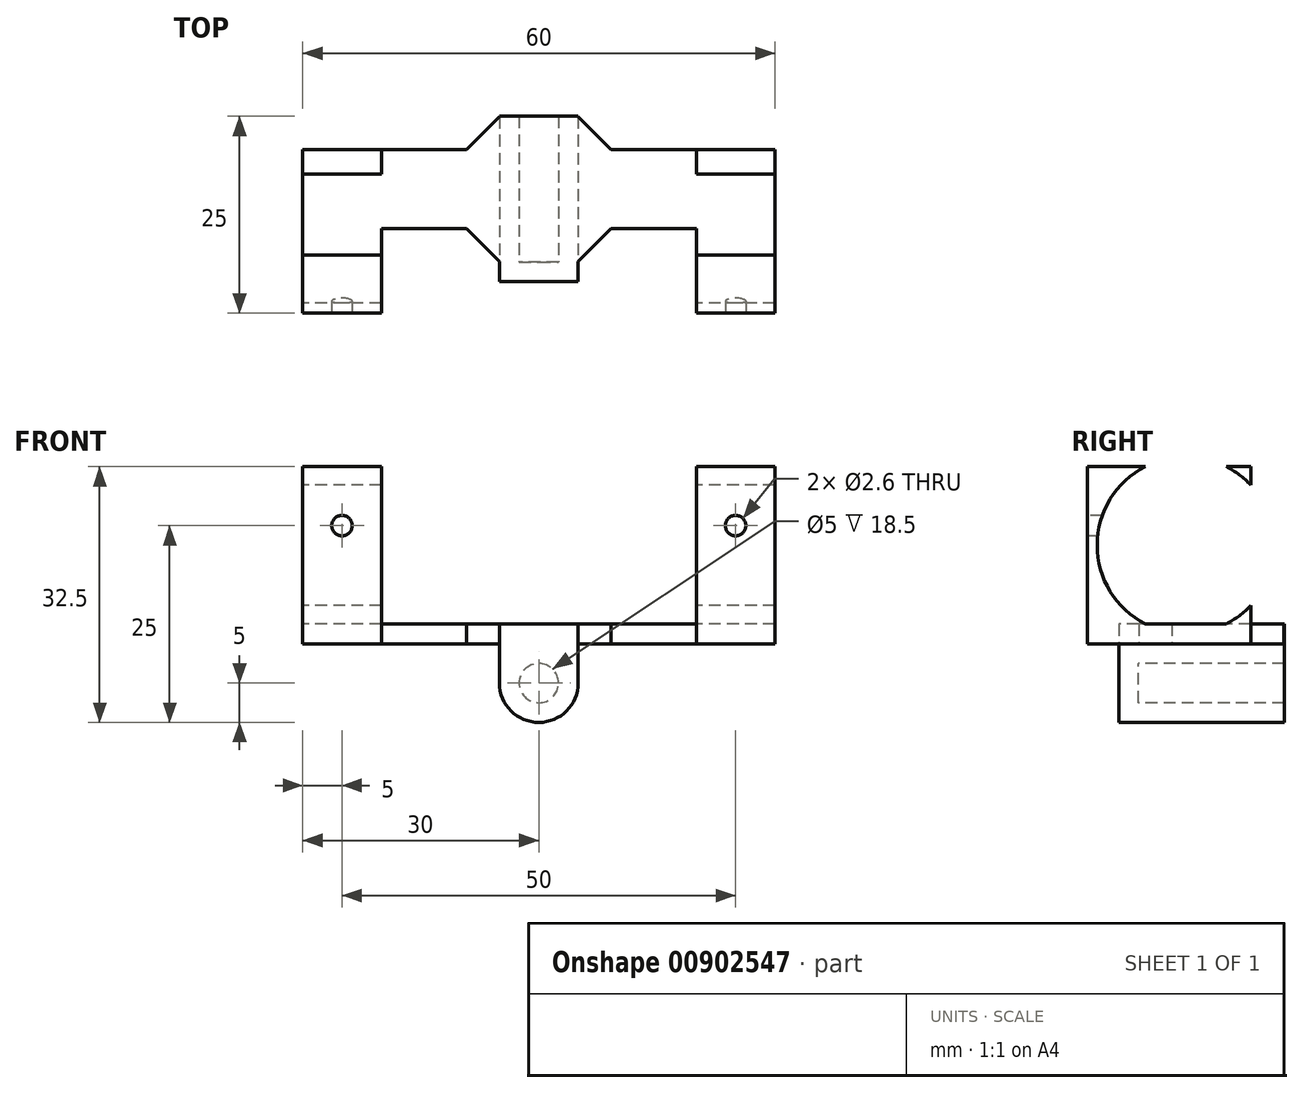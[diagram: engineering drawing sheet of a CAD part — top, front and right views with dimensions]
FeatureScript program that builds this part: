
annotation { "Feature Type Name" : "Feature", "Feature Type Description" : "" }
export const myFeature = defineFeature(function(context is Context, id is Id, definition is map)
    precondition{}
    {
        {
            var Q0;
            Q0=qCreatedBy(makeId("Top.planeOp"),FACE);
            var sketch = newSketch(context, id + "F0", { "sketchPlane" : qUnion([Q0])});
            skLineSegment(sketch, "E0.bottom", {"start": v(5, 9.25) * mm, "end": v(-5, 9.25) * mm});
            skLineSegment(sketch, "E0.top", {"start": v(5, -9.25) * mm, "end": v(-5, -9.25) * mm});
            skLineSegment(sketch, "E0.left", {"start": v(5, 9.25) * mm, "end": v(5, -9.25) * mm});
            skLineSegment(sketch, "E0.right", {"start": v(-5, 9.25) * mm, "end": v(-5, -9.25) * mm});
            skPoint(sketch, "E0.middle", {"position": v(0, 0) * mm});
            skLineSegment(sketch, "E1.bottom", {"start": v(30, 5) * mm, "end": v(-30, 5) * mm});
            skLineSegment(sketch, "E1.top", {"start": v(30, -5) * mm, "end": v(-30, -5) * mm});
            skLineSegment(sketch, "E1.left", {"start": v(30, 5) * mm, "end": v(30, -5) * mm});
            skLineSegment(sketch, "E1.right", {"start": v(-30, 5) * mm, "end": v(-30, -5) * mm});
            skSolve(sketch);
        }
        {
            var Q0;
            {var subQ5=sQuery(id+"F0.wireOp",EDGE,"E1.right");Q0=makeQuery(id+"F0.imprint","IMPRINT",FACE,{"disambiguationData":[TD([[makeQuery(id+"F0.imprint","IMPRINT",EDGE,{"derivedFrom":subQ5}),1.0]])]});}
            var Q1;
            {var subQ0=sQuery(id+"F0.wireOp",EDGE,"E0.bottom");Q1=makeQuery(id+"F0.imprint","IMPRINT",FACE,{"disambiguationData":[TD([[makeQuery(id+"F0.imprint","IMPRINT",EDGE,{"derivedFrom":subQ0}),1.0]])]});}
            var Q2;
            {var subQ0=sQuery(id+"F0.wireOp",EDGE,"E1.bottom");var subQ1=sQuery(id+"F0.wireOp",EDGE,"E0.left");var subQ2=makeQuery(id+"F0.imprint","INTERSECT",VERTEX,{"derivedFrom":[subQ1,subQ0]});Q2=makeQuery(id+"F0.imprint","IMPRINT",FACE,{"disambiguationData":[TD([[makeQuery(id+"F0.imprint","IMPRINT",EDGE,{"disambiguationData":[TD([[subQ2,-1.0]])],"derivedFrom":subQ1}),-1.0]])]});}
            var Q3;
            {var subQ0=sQuery(id+"F0.wireOp",EDGE,"E0.top");Q3=makeQuery(id+"F0.imprint","IMPRINT",FACE,{"disambiguationData":[TD([[makeQuery(id+"F0.imprint","IMPRINT",EDGE,{"derivedFrom":subQ0}),-1.0]])]});}
            var Q4;
            {var subQ5=sQuery(id+"F0.wireOp",EDGE,"E1.left");Q4=makeQuery(id+"F0.imprint","IMPRINT",FACE,{"disambiguationData":[TD([[makeQuery(id+"F0.imprint","IMPRINT",EDGE,{"derivedFrom":subQ5}),-1.0]])]});}
            extrude(context, id + "F1", {"entities" : qUnion([Q0, Q1, Q2, Q3, Q4]), "depth" : 2.5 * mm, "offsetDistance" : 25 * mm});
        }
        {
            var Q0;
            Q0=makeQuery(id+"F1.opExtrude","SWEPT_FACE",FACE,{"disambiguationData":[OSD([sQuery(id+"F0.wireOp",EDGE,"E0.top")])]});
            var sketch = newSketch(context, id + "F2", { "sketchPlane" : qUnion([Q0])});
            skLineSegment(sketch, "E2.bottom", {"start": v(-5, 0) * mm, "end": v(5, 0) * mm});
            skLineSegment(sketch, "E2.top", {"start": v(-5, -5) * mm, "end": v(5, -5) * mm});
            skLineSegment(sketch, "E2.left", {"start": v(-5, 0) * mm, "end": v(-5, -5) * mm});
            skLineSegment(sketch, "E2.right", {"start": v(5, 0) * mm, "end": v(5, -5) * mm});
            skCircle(sketch, "E3", {"center": v(0, -5) * mm, "radius": 5 * mm});
            skCircle(sketch, "E4", {"center": v(0, -5) * mm, "radius": 2.5 * mm});
            skSolve(sketch);
        }
        {
            var Q0;
            Q0=makeQuery(id+"F2.imprint","IMPRINT",FACE,{"disambiguationData":[TD([[makeQuery(id+"F2.imprint","IMPRINT",EDGE,{"derivedFrom":sQuery(id+"F2.wireOp",EDGE,"E2.bottom")}),1.0]])]});
            var Q1;
            {var subQ1=sQuery(id+"F2.wireOp",EDGE,"E2.top");var subQ3=sQuery(id+"F2.wireOp",EDGE,"E4");var subQ4=makeQuery(id+"F2.imprint","INTERSECT",VERTEX,{"disambiguationData":[OD(0.0)],"derivedFrom":[subQ1,subQ3]});Q1=makeQuery(id+"F2.imprint","IMPRINT",FACE,{"disambiguationData":[TD([[makeQuery(id+"F2.imprint","IMPRINT",EDGE,{"disambiguationData":[TD([[subQ4,1.0]])],"derivedFrom":subQ3}),-1.0]])]});}
            var Q2;
            {var subQ1=sQuery(id+"F2.wireOp",EDGE,"E2.top");var subQ3=sQuery(id+"F2.wireOp",EDGE,"E4");var subQ4=makeQuery(id+"F2.imprint","INTERSECT",VERTEX,{"disambiguationData":[OD(0.0)],"derivedFrom":[subQ1,subQ3]});Q2=makeQuery(id+"F2.imprint","IMPRINT",FACE,{"disambiguationData":[TD([[makeQuery(id+"F2.imprint","IMPRINT",EDGE,{"disambiguationData":[TD([[subQ4,-1.0]])],"derivedFrom":subQ3}),-1.0]])]});}
            var Q3;
            {var subQ0=sQuery(id+"F2.wireOp",EDGE,"E4");var subQ1=sQuery(id+"F2.wireOp",EDGE,"E2.top");var subQ2=makeQuery(id+"F2.imprint","INTERSECT",VERTEX,{"disambiguationData":[OD(0.0)],"derivedFrom":[subQ1,subQ0]});Q3=makeQuery(id+"F2.imprint","IMPRINT",FACE,{"disambiguationData":[TD([[makeQuery(id+"F2.imprint","IMPRINT",EDGE,{"disambiguationData":[TD([[subQ2,-1.0]])],"derivedFrom":subQ1}),-1.0]])]});}
            var Q4;
            {var subQ0=sQuery(id+"F2.wireOp",EDGE,"E4");var subQ1=sQuery(id+"F2.wireOp",EDGE,"E2.top");var subQ2=makeQuery(id+"F2.imprint","INTERSECT",VERTEX,{"disambiguationData":[OD(0.0)],"derivedFrom":[subQ1,subQ0]});Q4=makeQuery(id+"F2.imprint","IMPRINT",FACE,{"disambiguationData":[TD([[makeQuery(id+"F2.imprint","IMPRINT",EDGE,{"disambiguationData":[TD([[subQ2,-1.0]])],"derivedFrom":subQ1}),1.0]])]});}
            var Q5;
            Q5=makeQuery(id+"F2.imprint","IMPRINT",FACE,{"disambiguationData":[TD([[makeQuery(id+"F2.imprint","IMPRINT",EDGE,{"derivedFrom":sQuery(id+"F2.wireOp",EDGE,"E2.bottom")}),-1.0]])]});
            extrude(context, id + "F3", {"entities" : qUnion([Q0, Q1, Q2, Q3, Q4, Q5]), "operationType" : NewBodyOperationType.ADD, "depth" : 2.5 * mm, "offsetDistance" : 25 * mm});
        }
        {
            var Q0;
            {var subQ1=sQuery(id+"F2.wireOp",EDGE,"E2.top");var subQ3=sQuery(id+"F2.wireOp",EDGE,"E4");var subQ4=makeQuery(id+"F2.imprint","INTERSECT",VERTEX,{"disambiguationData":[OD(0.0)],"derivedFrom":[subQ1,subQ3]});Q0=makeQuery(id+"F2.imprint","IMPRINT",FACE,{"disambiguationData":[TD([[makeQuery(id+"F2.imprint","IMPRINT",EDGE,{"disambiguationData":[TD([[subQ4,1.0]])],"derivedFrom":subQ3}),-1.0]])]});}
            var Q1;
            {var subQ1=sQuery(id+"F2.wireOp",EDGE,"E2.top");var subQ3=sQuery(id+"F2.wireOp",EDGE,"E4");var subQ4=makeQuery(id+"F2.imprint","INTERSECT",VERTEX,{"disambiguationData":[OD(0.0)],"derivedFrom":[subQ1,subQ3]});Q1=makeQuery(id+"F2.imprint","IMPRINT",FACE,{"disambiguationData":[TD([[makeQuery(id+"F2.imprint","IMPRINT",EDGE,{"disambiguationData":[TD([[subQ4,-1.0]])],"derivedFrom":subQ3}),-1.0]])]});}
            var Q2;
            Q2=makeQuery(id+"F2.imprint","IMPRINT",FACE,{"disambiguationData":[TD([[makeQuery(id+"F2.imprint","IMPRINT",EDGE,{"derivedFrom":sQuery(id+"F2.wireOp",EDGE,"E2.bottom")}),1.0]])]});
            extrude(context, id + "F4", {"entities" : qUnion([Q0, Q1, Q2]), "operationType" : NewBodyOperationType.ADD, "oppositeDirection" : true, "depth" : 18.5 * mm, "offsetDistance" : 25 * mm});
        }
        {
            var Q0;
            Q0=makeQuery(id+"F1.opExtrude","SWEPT_EDGE",EDGE,{"disambiguationData":[OSD([sQuery(id+"F0.wireOp",EDGE,"E0.right"),sQuery(id+"F0.wireOp",EDGE,"E1.bottom")])]});
            var Q1;
            Q1=makeQuery(id+"F1.opExtrude","SWEPT_EDGE",EDGE,{"disambiguationData":[OSD([sQuery(id+"F0.wireOp",EDGE,"E0.right"),sQuery(id+"F0.wireOp",EDGE,"E1.top")])]});
            var Q2;
            Q2=makeQuery(id+"F1.opExtrude","SWEPT_EDGE",EDGE,{"disambiguationData":[OSD([sQuery(id+"F0.wireOp",EDGE,"E0.left"),sQuery(id+"F0.wireOp",EDGE,"E1.bottom")])]});
            var Q3;
            Q3=makeQuery(id+"F1.opExtrude","SWEPT_EDGE",EDGE,{"disambiguationData":[OSD([sQuery(id+"F0.wireOp",EDGE,"E0.left"),sQuery(id+"F0.wireOp",EDGE,"E1.top")])]});
            chamfer(context, id + "F5", {"entities" : qUnion([Q0, Q1, Q2, Q3]), "width" : 4.2 * mm, "tangentPropagation" : true});
        }
        {
            var Q0;
            {var subQ0=sQuery(id+"F0.wireOp",EDGE,"E0.top");Q0=makeQuery(id+"F3.boolean.opBoolean","MERGE",FACE,{"derivedFrom":[makeQuery(id+"F1.opExtrude","CAP_FACE",FACE,{"disambiguationData":[OSD([sQuery(id+"F0.wireOp",EDGE,"E0.bottom"),subQ0,sQuery(id+"F0.wireOp",EDGE,"E0.left"),sQuery(id+"F0.wireOp",EDGE,"E0.right"),sQuery(id+"F0.wireOp",EDGE,"E1.bottom"),sQuery(id+"F0.wireOp",EDGE,"E1.top"),sQuery(id+"F0.wireOp",EDGE,"E1.left"),sQuery(id+"F0.wireOp",EDGE,"E1.right")])],"isStart":false}),makeQuery(id+"F3.opExtrude","SWEPT_FACE",FACE,{"disambiguationData":[OSD([subQ0])]})]});}
            var sketch = newSketch(context, id + "F6", { "sketchPlane" : qUnion([Q0])});
            skLineSegment(sketch, "E5", {"start": v(0, 9.25) * mm, "end": v(-30, 9.25) * mm});
            skLineSegment(sketch, "E6.bottom", {"start": v(-30, 9.25) * mm, "end": v(-20, 9.25) * mm});
            skLineSegment(sketch, "E6.top", {"start": v(-30, -15.75) * mm, "end": v(-20, -15.75) * mm});
            skLineSegment(sketch, "E6.left", {"start": v(-30, 9.25) * mm, "end": v(-30, -15.75) * mm});
            skLineSegment(sketch, "E6.right", {"start": v(-20, 9.25) * mm, "end": v(-20, -15.75) * mm});
            skLineSegment(sketch, "E7", {"start": v(0, 9.25) * mm, "end": v(30, 9.25) * mm});
            skLineSegment(sketch, "E8.bottom", {"start": v(30, 9.25) * mm, "end": v(20, 9.25) * mm});
            skLineSegment(sketch, "E8.top", {"start": v(30, -15.75) * mm, "end": v(20, -15.75) * mm});
            skLineSegment(sketch, "E8.left", {"start": v(30, 9.25) * mm, "end": v(30, -15.75) * mm});
            skLineSegment(sketch, "E8.right", {"start": v(20, 9.25) * mm, "end": v(20, -15.75) * mm});
            skSolve(sketch);
        }
        {
            var Q0;
            {var subQ0=sQuery(id+"F6.wireOp",EDGE,"E6.bottom");Q0=makeQuery(id+"F6.imprint","IMPRINT",FACE,{"disambiguationData":[TD([[makeQuery(id+"F6.imprint","IMPRINT",EDGE,{"derivedFrom":subQ0}),-1.0]])]});}
            var Q1;
            {var subQ0=sQuery(id+"F6.wireOp",EDGE,"E6.left");var subQ1=sQuery(id+"F0.wireOp",EDGE,"E1.right");var subQ2=sQuery(id+"F0.wireOp",EDGE,"E1.bottom");var subQ4=makeQuery(id+"F1.opExtrude","CAP_EDGE",EDGE,{"disambiguationData":[OSD([subQ2]),TDD([makeQuery(id+"F0.imprint","IMPRINT",EDGE,{"disambiguationData":[TD([[makeQuery(id+"F0.imprint","INTERSECT",VERTEX,{"derivedFrom":[subQ2,subQ1]}),1.0]])],"derivedFrom":subQ2})])],"isStart":false});var subQ5=makeQuery(id+"F6.imprint","INTERSECT",VERTEX,{"derivedFrom":[subQ4,subQ0]});Q1=makeQuery(id+"F6.imprint","IMPRINT",FACE,{"disambiguationData":[TD([[makeQuery(id+"F6.imprint","IMPRINT",EDGE,{"disambiguationData":[TD([[subQ5,-1.0]])],"derivedFrom":subQ0}),1.0]])]});}
            var Q2;
            {var subQ0=sQuery(id+"F6.wireOp",EDGE,"E6.top");Q2=makeQuery(id+"F6.imprint","IMPRINT",FACE,{"disambiguationData":[TD([[makeQuery(id+"F6.imprint","IMPRINT",EDGE,{"derivedFrom":subQ0}),1.0]])]});}
            var Q3;
            {var subQ0=sQuery(id+"F6.wireOp",EDGE,"E8.bottom");Q3=makeQuery(id+"F6.imprint","IMPRINT",FACE,{"disambiguationData":[TD([[makeQuery(id+"F6.imprint","IMPRINT",EDGE,{"derivedFrom":subQ0}),1.0]])]});}
            var Q4;
            {var subQ0=sQuery(id+"F6.wireOp",EDGE,"E8.left");var subQ1=sQuery(id+"F0.wireOp",EDGE,"E1.left");var subQ2=sQuery(id+"F0.wireOp",EDGE,"E1.bottom");var subQ4=makeQuery(id+"F1.opExtrude","CAP_EDGE",EDGE,{"disambiguationData":[OSD([subQ2]),TDD([makeQuery(id+"F0.imprint","IMPRINT",EDGE,{"disambiguationData":[TD([[makeQuery(id+"F0.imprint","INTERSECT",VERTEX,{"derivedFrom":[subQ2,subQ1]}),-1.0]])],"derivedFrom":subQ2})])],"isStart":false});var subQ5=makeQuery(id+"F6.imprint","INTERSECT",VERTEX,{"derivedFrom":[subQ4,subQ0]});Q4=makeQuery(id+"F6.imprint","IMPRINT",FACE,{"disambiguationData":[TD([[makeQuery(id+"F6.imprint","IMPRINT",EDGE,{"disambiguationData":[TD([[subQ5,-1.0]])],"derivedFrom":subQ0}),-1.0]])]});}
            var Q5;
            {var subQ0=sQuery(id+"F6.wireOp",EDGE,"E8.top");Q5=makeQuery(id+"F6.imprint","IMPRINT",FACE,{"disambiguationData":[TD([[makeQuery(id+"F6.imprint","IMPRINT",EDGE,{"derivedFrom":subQ0}),-1.0]])]});}
            extrude(context, id + "F7", {"entities" : qUnion([Q0, Q1, Q2, Q3, Q4, Q5]), "operationType" : NewBodyOperationType.ADD, "oppositeDirection" : true, "depth" : 2.5 * mm, "offsetDistance" : 25 * mm});
        }
        {
            var Q0;
            {var subQ0=sQuery(id+"F6.wireOp",EDGE,"E6.bottom");Q0=makeQuery(id+"F6.imprint","IMPRINT",FACE,{"disambiguationData":[TD([[makeQuery(id+"F6.imprint","IMPRINT",EDGE,{"derivedFrom":subQ0}),-1.0]])]});}
            var Q1;
            {var subQ0=sQuery(id+"F6.wireOp",EDGE,"E6.left");var subQ1=sQuery(id+"F0.wireOp",EDGE,"E1.right");var subQ2=sQuery(id+"F0.wireOp",EDGE,"E1.bottom");var subQ4=makeQuery(id+"F1.opExtrude","CAP_EDGE",EDGE,{"disambiguationData":[OSD([subQ2]),TDD([makeQuery(id+"F0.imprint","IMPRINT",EDGE,{"disambiguationData":[TD([[makeQuery(id+"F0.imprint","INTERSECT",VERTEX,{"derivedFrom":[subQ2,subQ1]}),1.0]])],"derivedFrom":subQ2})])],"isStart":false});var subQ5=makeQuery(id+"F6.imprint","INTERSECT",VERTEX,{"derivedFrom":[subQ4,subQ0]});Q1=makeQuery(id+"F6.imprint","IMPRINT",FACE,{"disambiguationData":[TD([[makeQuery(id+"F6.imprint","IMPRINT",EDGE,{"disambiguationData":[TD([[subQ5,-1.0]])],"derivedFrom":subQ0}),1.0]])]});}
            var Q2;
            {var subQ0=sQuery(id+"F6.wireOp",EDGE,"E6.top");Q2=makeQuery(id+"F6.imprint","IMPRINT",FACE,{"disambiguationData":[TD([[makeQuery(id+"F6.imprint","IMPRINT",EDGE,{"derivedFrom":subQ0}),1.0]])]});}
            var Q3;
            {var subQ0=sQuery(id+"F6.wireOp",EDGE,"E8.top");Q3=makeQuery(id+"F6.imprint","IMPRINT",FACE,{"disambiguationData":[TD([[makeQuery(id+"F6.imprint","IMPRINT",EDGE,{"derivedFrom":subQ0}),-1.0]])]});}
            var Q4;
            {var subQ0=sQuery(id+"F6.wireOp",EDGE,"E8.left");var subQ1=sQuery(id+"F0.wireOp",EDGE,"E1.left");var subQ2=sQuery(id+"F0.wireOp",EDGE,"E1.bottom");var subQ4=makeQuery(id+"F1.opExtrude","CAP_EDGE",EDGE,{"disambiguationData":[OSD([subQ2]),TDD([makeQuery(id+"F0.imprint","IMPRINT",EDGE,{"disambiguationData":[TD([[makeQuery(id+"F0.imprint","INTERSECT",VERTEX,{"derivedFrom":[subQ2,subQ1]}),-1.0]])],"derivedFrom":subQ2})])],"isStart":false});var subQ5=makeQuery(id+"F6.imprint","INTERSECT",VERTEX,{"derivedFrom":[subQ4,subQ0]});Q4=makeQuery(id+"F6.imprint","IMPRINT",FACE,{"disambiguationData":[TD([[makeQuery(id+"F6.imprint","IMPRINT",EDGE,{"disambiguationData":[TD([[subQ5,-1.0]])],"derivedFrom":subQ0}),-1.0]])]});}
            var Q5;
            {var subQ0=sQuery(id+"F6.wireOp",EDGE,"E8.bottom");Q5=makeQuery(id+"F6.imprint","IMPRINT",FACE,{"disambiguationData":[TD([[makeQuery(id+"F6.imprint","IMPRINT",EDGE,{"derivedFrom":subQ0}),1.0]])]});}
            extrude(context, id + "F8", {"entities" : qUnion([Q0, Q1, Q2, Q3, Q4, Q5]), "operationType" : NewBodyOperationType.ADD, "depth" : 20 * mm, "offsetDistance" : 25 * mm});
        }
        {
            var Q0;
            {var subQ0=sQuery(id+"F6.wireOp",EDGE,"E6.left");Q0=makeQuery(id+"F8.boolean.opBoolean","MERGE",FACE,{"derivedFrom":[makeQuery(id+"F7.boolean.opBoolean","MERGE",FACE,{"derivedFrom":[makeQuery(id+"F1.opExtrude","SWEPT_FACE",FACE,{"disambiguationData":[OSD([sQuery(id+"F0.wireOp",EDGE,"E1.right")])]}),makeQuery(id+"F7.opExtrude","SWEPT_FACE",FACE,{"disambiguationData":[OSD([subQ0])]})]}),makeQuery(id+"F8.opExtrude","SWEPT_FACE",FACE,{"disambiguationData":[OSD([subQ0])]})]});}
            var sketch = newSketch(context, id + "F9", { "sketchPlane" : qUnion([Q0])});
            skLineSegment(sketch, "E9", {"start": v(3.25, 22.5) * mm, "end": v(3.25, 12.5) * mm});
            skCircle(sketch, "E10", {"center": v(3.25, 12.5) * mm, "radius": 11.25 * mm});
            skLineSegment(sketch, "E11.bottom", {"start": v(14.5, 22.5) * mm, "end": v(-8, 22.5) * mm});
            skLineSegment(sketch, "E11.top", {"start": v(14.5, 2.5) * mm, "end": v(-8, 2.5) * mm});
            skLineSegment(sketch, "E11.left", {"start": v(14.5, 22.5) * mm, "end": v(14.5, 2.5) * mm});
            skLineSegment(sketch, "E11.right", {"start": v(-8, 22.5) * mm, "end": v(-8, 2.5) * mm});
            skSolve(sketch);
        }
        {
            var Q0;
            {var subQ4=sQuery(id+"F9.wireOp",EDGE,"E11.bottom");var subQ9=makeQuery(id+"F9.imprint","IMPRINT",VERTEX,{"derivedFrom":subQ4});Q0=makeQuery(id+"F9.imprint","IMPRINT",FACE,{"disambiguationData":[TD([[makeQuery(id+"F9.imprint","IMPRINT",EDGE,{"disambiguationData":[TD([[subQ9,1.0]])],"derivedFrom":subQ4}),-1.0]])]});}
            var Q1;
            {var subQ0=sQuery(id+"F9.wireOp",EDGE,"E11.bottom");var subQ1=sQuery(id+"F9.wireOp",EDGE,"E10");var subQ2=makeQuery(id+"F9.imprint","INTERSECT",VERTEX,{"disambiguationData":[OD(1.0)],"derivedFrom":[subQ1,subQ0]});Q1=makeQuery(id+"F9.imprint","IMPRINT",FACE,{"disambiguationData":[TD([[makeQuery(id+"F9.imprint","IMPRINT",EDGE,{"disambiguationData":[TD([[subQ2,-1.0]])],"derivedFrom":subQ1}),-1.0]])]});}
            var Q2;
            {var subQ0=sQuery(id+"F9.wireOp",EDGE,"E11.bottom");var subQ1=sQuery(id+"F9.wireOp",EDGE,"E10");var subQ2=makeQuery(id+"F9.imprint","INTERSECT",VERTEX,{"disambiguationData":[OD(0.0)],"derivedFrom":[subQ1,subQ0]});Q2=makeQuery(id+"F9.imprint","IMPRINT",FACE,{"disambiguationData":[TD([[makeQuery(id+"F9.imprint","IMPRINT",EDGE,{"disambiguationData":[TD([[subQ2,1.0]])],"derivedFrom":subQ1}),-1.0]])]});}
            extrude(context, id + "F10", {"entities" : qUnion([Q0, Q1, Q2]), "operationType" : NewBodyOperationType.REMOVE, "oppositeDirection" : true, "depth" : 60 * mm, "offsetDistance" : 25 * mm});
        }
        {
            var Q0;
            {var subQ0=sQuery(id+"F6.wireOp",EDGE,"E6.top");Q0=makeQuery(id+"F8.boolean.opBoolean","MERGE",FACE,{"derivedFrom":[makeQuery(id+"F7.opExtrude","SWEPT_FACE",FACE,{"disambiguationData":[OSD([subQ0])]}),makeQuery(id+"F8.opExtrude","SWEPT_FACE",FACE,{"disambiguationData":[OSD([subQ0])]})]});}
            var sketch = newSketch(context, id + "F11", { "sketchPlane" : qUnion([Q0])});
            skLineSegment(sketch, "E12", {"start": v(-25, 22.5) * mm, "end": v(-25, 15) * mm});
            skCircle(sketch, "E13", {"center": v(-25, 15) * mm, "radius": 1.3 * mm});
            skLineSegment(sketch, "E14", {"start": v(-25, 15) * mm, "end": v(25, 15) * mm});
            skCircle(sketch, "E15", {"center": v(25, 15) * mm, "radius": 1.3 * mm});
            skSolve(sketch);
        }
        {
            var Q0;
            {var subQ0=sQuery(id+"F11.wireOp",EDGE,"E14");var subQ1=sQuery(id+"F11.wireOp",EDGE,"E12");var subQ2=makeQuery(id+"F11.imprint","INTERSECT",VERTEX,{"derivedFrom":[subQ1,subQ0]});Q0=makeQuery(id+"F11.imprint","IMPRINT",FACE,{"disambiguationData":[TD([[makeQuery(id+"F11.imprint","IMPRINT",EDGE,{"disambiguationData":[TD([[subQ2,1.0]])],"derivedFrom":subQ1}),-1.0]])]});}
            var Q1;
            {var subQ0=sQuery(id+"F11.wireOp",EDGE,"E14");var subQ1=sQuery(id+"F11.wireOp",EDGE,"E12");var subQ2=makeQuery(id+"F11.imprint","INTERSECT",VERTEX,{"derivedFrom":[subQ1,subQ0]});Q1=makeQuery(id+"F11.imprint","IMPRINT",FACE,{"disambiguationData":[TD([[makeQuery(id+"F11.imprint","IMPRINT",EDGE,{"disambiguationData":[TD([[subQ2,1.0]])],"derivedFrom":subQ1}),1.0]])]});}
            var Q2;
            Q2=makeQuery(id+"F11.imprint","IMPRINT",FACE,{"disambiguationData":[TD([[makeQuery(id+"F11.imprint","IMPRINT",EDGE,{"derivedFrom":sQuery(id+"F11.wireOp",EDGE,"E15")}),1.0]])]});
            extrude(context, id + "F12", {"entities" : qUnion([Q0, Q1, Q2]), "operationType" : NewBodyOperationType.REMOVE, "oppositeDirection" : true, "depth" : 10 * mm, "offsetDistance" : 25 * mm});
        }
    });
